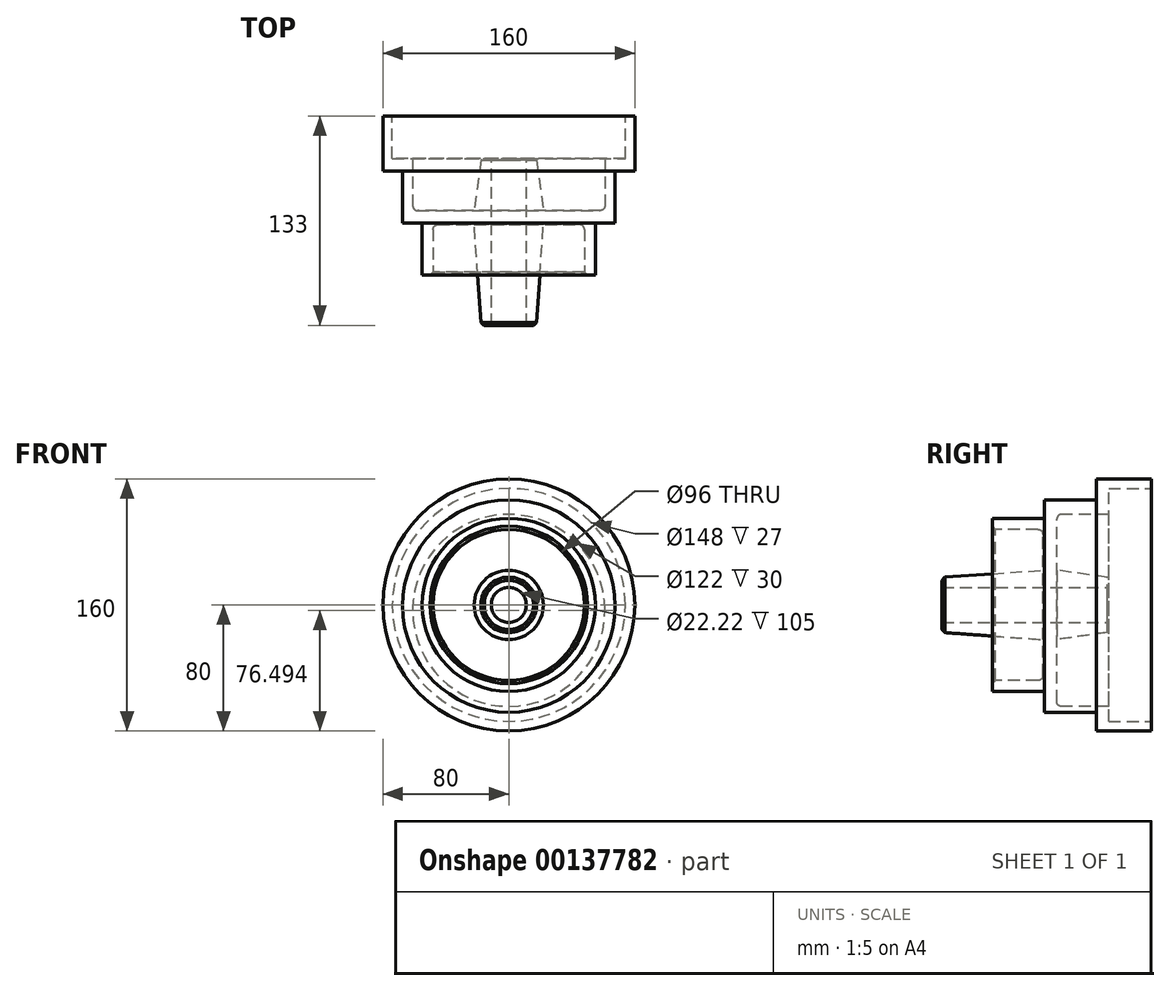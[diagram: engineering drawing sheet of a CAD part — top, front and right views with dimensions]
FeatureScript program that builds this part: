
annotation { "Feature Type Name" : "Feature", "Feature Type Description" : "" }
export const myFeature = defineFeature(function(context is Context, id is Id, definition is map)
    precondition{}
    {
        {
            var Q0;
            Q0=qCreatedBy(makeId("Front.planeOp"),FACE);
            cPlane(context, id + "F0", {"entities" : qUnion([Q0]), "cplaneType" : CPlaneType.OFFSET, "offset" : 133 * mm, "width" : 150 * mm, "height" : 150 * mm});
        }
        {
            var Q0;
            Q0=qCreatedBy(id+"F0.planeOp",FACE);
            cPlane(context, id + "F1", {"entities" : qUnion([Q0]), "cplaneType" : CPlaneType.OFFSET, "offset" : 73 * mm, "oppositeDirection" : true, "width" : 150 * mm, "height" : 150 * mm});
        }
        {
            var Q0;
            Q0=qCreatedBy(id+"F1.planeOp",FACE);
            cPlane(context, id + "F2", {"entities" : qUnion([Q0]), "cplaneType" : CPlaneType.OFFSET, "offset" : 32 * mm, "oppositeDirection" : true, "width" : 150 * mm, "height" : 150 * mm});
        }
        {
            var Q0;
            Q0=qCreatedBy(makeId("Front.planeOp"),FACE);
            var sketch = newSketch(context, id + "F3", { "sketchPlane" : qUnion([Q0])});
            skCircle(sketch, "E0", {"center": v(0, 0) * mm, "radius": 80 * mm});
            skSolve(sketch);
        }
        {
            var Q0;
            Q0 = qSketchRegion(id + "F3", true);
            extrude(context, id + "F4", {"entities" : qUnion([Q0]), "depth" : 35 * mm});
        }
        {
            var Q0;
            Q0=makeQuery(id+"F4.opExtrude","CAP_FACE",FACE,{"disambiguationData":[OSD([sQuery(id+"F3.wireOp",EDGE,"E0")])],"isStart":false});
            var sketch = newSketch(context, id + "F5", { "sketchPlane" : qUnion([Q0])});
            skCircle(sketch, "E1", {"center": v(0, -0.73) * mm, "radius": 67.5 * mm});
            skSolve(sketch);
        }
        {
            var Q0;
            Q0 = qSketchRegion(id + "F5", true);
            extrude(context, id + "F6", {"entities" : qUnion([Q0]), "operationType" : NewBodyOperationType.ADD, "depth" : 33 * mm});
        }
        {
            var Q0;
            Q0=makeQuery(id+"F6.opExtrude","CAP_FACE",FACE,{"disambiguationData":[OSD([sQuery(id+"F5.wireOp",EDGE,"E1")])],"isStart":false});
            var sketch = newSketch(context, id + "F7", { "sketchPlane" : qUnion([Q0])});
            skCircle(sketch, "E2", {"center": v(0, 0) * mm, "radius": 55 * mm});
            skSolve(sketch);
        }
        {
            var Q0;
            Q0 = qSketchRegion(id + "F7", true);
            extrude(context, id + "F8", {"entities" : qUnion([Q0]), "operationType" : NewBodyOperationType.ADD, "depth" : 33 * mm});
        }
        {
            var Q0;
            Q0=qCreatedBy(id+"F0.planeOp",FACE);
            var sketch = newSketch(context, id + "F9", { "sketchPlane" : qUnion([Q0])});
            skCircle(sketch, "E3", {"center": v(0, 0) * mm, "radius": 48 * mm});
            skSolve(sketch);
        }
        {
            var Q0;
            Q0 = qSketchRegion(id + "F9", true);
            extrude(context, id + "F10", {"entities" : qUnion([Q0]), "operationType" : NewBodyOperationType.REMOVE, "oppositeDirection" : true, "depth" : 64 * mm});
        }
        {
            var Q0;
            Q0=makeQuery(id+"F10.boolean.opBoolean","COPY",FACE,{"derivedFrom":makeQuery(id+"F10.opExtrude","CAP_FACE",FACE,{"disambiguationData":[OSD([sQuery(id+"F9.wireOp",EDGE,"E3")])],"isStart":false})});
            var sketch = newSketch(context, id + "F11", { "sketchPlane" : qUnion([Q0])});
            skCircle(sketch, "E4", {"center": v(0, 0) * mm, "radius": 22 * mm});
            skSolve(sketch);
        }
        {
            var Q0;
            Q0=qCreatedBy(id+"F0.planeOp",FACE);
            var sketch = newSketch(context, id + "F12", { "sketchPlane" : qUnion([Q0])});
            skCircle(sketch, "E5", {"center": v(0, 0) * mm, "radius": 17.5 * mm});
            skSolve(sketch);
        }
        {
            var Q1;
            Q1 = qSketchRegion(id + "F11", true);
            var Q2;
            Q2 = qSketchRegion(id + "F12", true);
            loft(context, id + "F13", {"operationType" : NewBodyOperationType.ADD, "sheetProfilesArray" : [{ "sheetProfileEntities" : qUnion([Q1]) }, { "sheetProfileEntities" : qUnion([Q2]) }]});
        }
        {
            var Q0;
            Q0=qCreatedBy(makeId("Front.planeOp"),FACE);
            var sketch = newSketch(context, id + "F14", { "sketchPlane" : qUnion([Q0])});
            skCircle(sketch, "E6", {"center": v(0, 0) * mm, "radius": 74 * mm});
            skSolve(sketch);
        }
        {
            var Q0;
            Q0 = qSketchRegion(id + "F14", true);
            extrude(context, id + "F15", {"entities" : qUnion([Q0]), "operationType" : NewBodyOperationType.REMOVE, "depth" : 27 * mm});
        }
        {
            var Q0;
            Q0=qCreatedBy(id+"F1.planeOp",FACE);
            var sketch = newSketch(context, id + "F16", { "sketchPlane" : qUnion([Q0])});
            skCircle(sketch, "E7", {"center": v(0, -3.5) * mm, "radius": 61 * mm});
            skSolve(sketch);
        }
        {
            var Q0;
            Q0 = qSketchRegion(id + "F16", true);
            extrude(context, id + "F17", {"entities" : qUnion([Q0]), "operationType" : NewBodyOperationType.REMOVE, "endBound" : BoundingType.THROUGH_ALL, "oppositeDirection" : true, "depth" : 25 * mm});
        }
        {
            var Q0;
            Q0=makeQuery(id+"F17.boolean.opBoolean","COPY",FACE,{"derivedFrom":makeQuery(id+"F17.opExtrude","CAP_FACE",FACE,{"disambiguationData":[OSD([sQuery(id+"F16.wireOp",EDGE,"E7")])],"isStart":true})});
            var sketch = newSketch(context, id + "F18", { "sketchPlane" : qUnion([Q0])});
            skCircle(sketch, "E8", {"center": v(0, 0) * mm, "radius": 22 * mm});
            skSolve(sketch);
        }
        {
            var Q0;
            Q0=qCreatedBy(id+"F2.planeOp",FACE);
            var sketch = newSketch(context, id + "F19", { "sketchPlane" : qUnion([Q0])});
            skCircle(sketch, "E9", {"center": v(0, 0) * mm, "radius": 17.5 * mm});
            skSolve(sketch);
        }
        {
            var Q1;
            Q1 = qSketchRegion(id + "F18", true);
            var Q2;
            Q2 = qSketchRegion(id + "F19", true);
            loft(context, id + "F20", {"operationType" : NewBodyOperationType.ADD, "sheetProfilesArray" : [{ "sheetProfileEntities" : qUnion([Q1]) }, { "sheetProfileEntities" : qUnion([Q2]) }]});
        }
        {
            var Q0;
            Q0=qCreatedBy(makeId("Front.planeOp"),FACE);
            var sketch = newSketch(context, id + "F21", { "sketchPlane" : qUnion([Q0])});
            skCircle(sketch, "E10", {"center": v(0, 0) * mm, "radius": 11.1 * mm});
            skSolve(sketch);
        }
        {
            var Q0;
            Q0 = qSketchRegion(id + "F21", true);
            extrude(context, id + "F22", {"entities" : qUnion([Q0]), "operationType" : NewBodyOperationType.REMOVE, "endBound" : BoundingType.THROUGH_ALL, "depth" : 25 * mm});
        }
        {
            var Q0;
            Q0=makeQuery(id+"F10.boolean.opBoolean","INTERSECT",EDGE,{"derivedFrom":[makeQuery(id+"F8.opExtrude","CAP_FACE",FACE,{"disambiguationData":[OSD([sQuery(id+"F7.wireOp",EDGE,"E2")])],"isStart":false}),makeQuery(id+"F10.opExtrude","SWEPT_FACE",FACE,{"disambiguationData":[OSD([sQuery(id+"F9.wireOp",EDGE,"E3")])]})]});
            var Q1;
            Q1=makeQuery(id+"F13.opLoft","MID_CAP_EDGE",EDGE,{"disambiguationData":[OSD([sQuery(id+"F11.wireOp",EDGE,"E4"),sQuery(id+"F12.wireOp",EDGE,"E5")])],"capPos":1.0});
            chamfer(context, id + "F23", {"entities" : qUnion([Q0, Q1]), "chamferType" : ChamferType.OFFSET_ANGLE, "width" : 2 * mm, "oppositeDirection" : false, "angle" : 45 * degree, "tangentPropagation" : true});
        }
        {
            var Q0;
            Q0=makeQuery(id+"F13.opLoft","MID_CAP_EDGE",EDGE,{"disambiguationData":[OSD([sQuery(id+"F11.wireOp",EDGE,"E4")])],"capPos":0.0});
            var Q1;
            Q1=makeQuery(id+"F10.boolean.opBoolean","COPY",EDGE,{"derivedFrom":makeQuery(id+"F10.opExtrude","CAP_EDGE",EDGE,{"disambiguationData":[OSD([sQuery(id+"F9.wireOp",EDGE,"E3")])],"isStart":false})});
            var Q2;
            Q2=makeQuery(id+"F17.boolean.opBoolean","COPY",EDGE,{"derivedFrom":makeQuery(id+"F17.opExtrude","CAP_EDGE",EDGE,{"disambiguationData":[OSD([sQuery(id+"F16.wireOp",EDGE,"E7")])],"isStart":true})});
            var Q3;
            Q3=makeQuery(id+"F20.opLoft","MID_CAP_EDGE",EDGE,{"disambiguationData":[OSD([sQuery(id+"F18.wireOp",EDGE,"E8")])],"capPos":0.0});
            fillet(context, id + "F24", {"entities" : qUnion([Q0, Q1, Q2, Q3]), "radius" : 3 * mm, "tangentPropagation" : true, "allowEdgeOverflow" : false});
        }
    });
